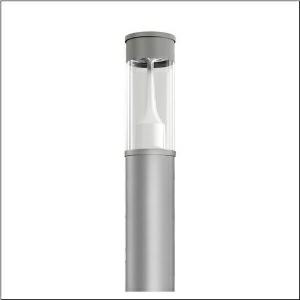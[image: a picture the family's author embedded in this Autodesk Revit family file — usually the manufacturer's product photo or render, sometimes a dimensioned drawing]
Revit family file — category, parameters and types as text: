
# Revit family: city-light_400_iq___st1_2a_5xa5305mf14hp_fa50
name_source: partatom
category: Lighting Fixtures
units: mm (PartAtom-declared; Revit-internal decimal feet)

## family parameters
Cut with Voids When Loaded = No
Host = Face
Light Source = No
Part Type = Normal
Room Calculation Point = No
Round Connector Dimension = Use Diameter
Shared = No

## types (1)
- --- (1 x LED, 4240 lm, 33.6 W, 2700K)
    Apparent Load = 34 VA
    CIE Flux Codes = 22 61 94 96 100
    Color Rendering = 70
    Color Temperature = 2700K
    Default Elevation = 1800 mm
    Description = City-Light 400 iQ, light pillar, Module 540 iQ-SR, primary light control with 3 zone facetted reflector, of plastic, silver coated, highly specular, structured, primary optical cover: cover, of PMMA, transparent, partly coated, light distribution: ST1.2a, primary light characteristic: asymmetric, LED, High Power LED, rated luminous flux: 4.240lm, luminous efficacy: 126lm/W, light colour: 727, colour temperature: 2700K, control gear: iQ Street-Remote, control: pre-setting: logarithmic dimming characteristic, Street-Remote, Auto-Match, Temp-Guard, Lumen-Switch, Night-Set, Smart-Wire, Light-Fading, Desk-Remote (wireless, voltage-free reading and setting of iQ features in the workshop via application-optimized NFC function/RFID function), optimised constant luminous flux control (CLO 2.0), with terminal, 6-pole, max. 2.5mm², mains connection: 230..240V, AC, 50/60Hz, start of lifetime: 34W, end of service life: 36W, reduction: 15W, luminaire housing, cylindrical, of extruded aluminium section, coated, Siteco® metallic grey (DB 702S), length: 4.694mm, diameter: 200mm, Module 540 iQ-SR, traffic white (RAL 9016), equipment: Power, protection rating (complete): IP65, insulation class (complete): insulation class II (safety insulation), certification: CE, ENEC, VDE, packaging unit: 1 piece

Light Distribution: ST1.2a
    Height = 500 mm
    Lamp = 1 x LED
    Lamp Light Flux = 4240 lm
    Lamp Power = 33.6 W
    Lamp count = 1
    Length = 200 mm
    Luminous efficacy = 126 lm/W
    Manufacturer = Siteco
    ModVariant = No
    Model = 5XA5305MF14HP
    Mounting Place = Floor
    Mounting Type = Freestanding
    Number of Poles = 1
    OnlyDefault = Yes
    Power Factor = 1
    Product Name = City-Light 400 iQ | ST1.2a
    Product group = light pillar
    ProductGroupID = 1301
    Protection Class = Protection class II
    Protection Degree = IP 65
    RLX_Detail_Level = 1
    RLX_Emergency_Light_Flux = 0 lm
    RLX_Emergency_Type = 0
    RLX_Emergency_Type_DB = No
    RlxData = <blob elided: 53397 chars, md5=fd984ca3>
    Socket = socket
    Standby Power = 0 W
    System Light Flux = 4240 lm
    System Power = 34 W
    Type Comments = factory setting: luminous flux: 100 % | dim-lin: 254 | 695 mA
    Type Image = l_1006916.jpg
    URL = http://relux.com
    VarID = @adj_151995
    Voltage = 0 V
    Weight = 0.00 kg
    Width = 0 mm  [stored 0 ft]

note: [stored X ft] marks values corroborated as IEEE doubles in the binary element streams (Revit-internal decimal feet)

## geometry (parser evidence)
native form markers: Blend x4, Sweep x9
no freeform markers — native parametric forms only
